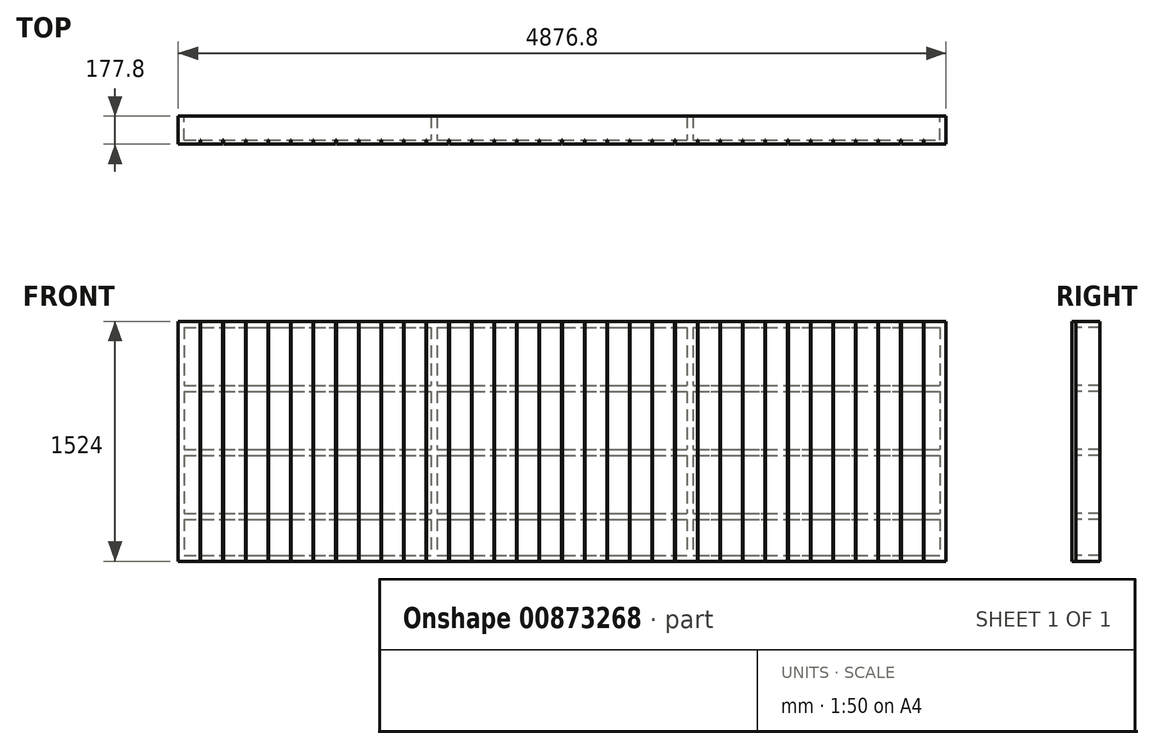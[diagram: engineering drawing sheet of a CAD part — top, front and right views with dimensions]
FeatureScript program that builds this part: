
annotation { "Feature Type Name" : "Feature", "Feature Type Description" : "" }
export const myFeature = defineFeature(function(context is Context, id is Id, definition is map)
    precondition{}
    {
        {
            var Q0;
            Q0=qCreatedBy(makeId("Front.planeOp"),FACE);
            var sketch = newSketch(context, id + "F0", { "sketchPlane" : qUnion([Q0])});
            skLineSegment(sketch, "E0.bottom", {"start": v(0, 0) * mm, "end": v(4876.8, 0) * mm});
            skLineSegment(sketch, "E0.top", {"start": v(0, -1524) * mm, "end": v(4876.8, -1524) * mm});
            skLineSegment(sketch, "E0.left", {"start": v(0, 0) * mm, "end": v(0, -1524) * mm});
            skLineSegment(sketch, "E0.right", {"start": v(4876.8, 0) * mm, "end": v(4876.8, -1524) * mm});
            skLineSegment(sketch, "E1.bottom", {"start": v(38.1, -38.1) * mm, "end": v(4838.7, -38.1) * mm});
            skLineSegment(sketch, "E1.top", {"start": v(38.1, -406.4) * mm, "end": v(4838.7, -406.4) * mm});
            skLineSegment(sketch, "E1.left", {"start": v(38.1, -38.1) * mm, "end": v(38.1, -406.4) * mm});
            skLineSegment(sketch, "E1.right", {"start": v(4838.7, -38.1) * mm, "end": v(4838.7, -406.4) * mm});
            skLineSegment(sketch, "E2", {"start": v(0, -425.45) * mm, "end": v(4876.8, -425.45) * mm, "construction": true});
            skLineSegment(sketch, "E3", {"start": v(4876.8, -19.05) * mm, "end": v(0, -19.05) * mm, "construction": true});
            skLineSegment(sketch, "E4.0.1.0", {"start": v(38.1, -812.8) * mm, "end": v(4838.7, -812.8) * mm});
            skLineSegment(sketch, "E4.0.1.1", {"start": v(38.1, -444.5) * mm, "end": v(38.1, -812.8) * mm});
            skLineSegment(sketch, "E4.0.1.2", {"start": v(38.1, -444.5) * mm, "end": v(4838.7, -444.5) * mm});
            skLineSegment(sketch, "E4.0.1.3", {"start": v(4838.7, -444.5) * mm, "end": v(4838.7, -812.8) * mm});
            skLineSegment(sketch, "E4.0.2.0", {"start": v(38.1, -1219.2) * mm, "end": v(4838.7, -1219.2) * mm});
            skLineSegment(sketch, "E4.0.2.1", {"start": v(38.1, -850.9) * mm, "end": v(38.1, -1219.2) * mm});
            skLineSegment(sketch, "E4.0.2.2", {"start": v(38.1, -850.9) * mm, "end": v(4838.7, -850.9) * mm});
            skLineSegment(sketch, "E4.0.2.3", {"start": v(4838.7, -850.9) * mm, "end": v(4838.7, -1219.2) * mm});
            skLineSegment(sketch, "E4.direction1", {"start": v(38.1, -406.4) * mm, "end": v(63.5, -406.4) * mm, "construction": true});
            skLineSegment(sketch, "E4.direction2", {"start": v(38.1, -406.4) * mm, "end": v(38.1, -812.8) * mm, "construction": true});
            skLineSegment(sketch, "E5.bottom", {"start": v(38.1, -1257.3) * mm, "end": v(4838.7, -1257.3) * mm});
            skLineSegment(sketch, "E5.top", {"start": v(38.1, -1485.9) * mm, "end": v(4838.7, -1485.9) * mm});
            skLineSegment(sketch, "E5.left", {"start": v(38.1, -1257.3) * mm, "end": v(38.1, -1485.9) * mm});
            skLineSegment(sketch, "E5.right", {"start": v(4838.7, -1257.3) * mm, "end": v(4838.7, -1485.9) * mm});
            skSolve(sketch);
        }
        {
            var Q0;
            Q0 = qSketchRegion(id + "F0", true);
            extrude(context, id + "F1", {"entities" : qUnion([Q0]), "depth" : 152.4 * mm, "offsetDistance" : 25.4 * mm});
        }
        {
            var Q0;
            Q0=makeQuery(id+"F1.opExtrude","CAP_FACE",FACE,{"disambiguationData":[OSD([sQuery(id+"F0.wireOp",EDGE,"E0.bottom"),sQuery(id+"F0.wireOp",EDGE,"E0.top"),sQuery(id+"F0.wireOp",EDGE,"E0.left"),sQuery(id+"F0.wireOp",EDGE,"E0.right"),sQuery(id+"F0.wireOp",EDGE,"E1.bottom"),sQuery(id+"F0.wireOp",EDGE,"E1.top"),sQuery(id+"F0.wireOp",EDGE,"E1.left"),sQuery(id+"F0.wireOp",EDGE,"E1.right"),sQuery(id+"F0.wireOp",EDGE,"E4.0.1.0"),sQuery(id+"F0.wireOp",EDGE,"E4.0.1.1"),sQuery(id+"F0.wireOp",EDGE,"E4.0.1.2"),sQuery(id+"F0.wireOp",EDGE,"E4.0.1.3"),sQuery(id+"F0.wireOp",EDGE,"E4.0.2.0"),sQuery(id+"F0.wireOp",EDGE,"E4.0.2.1"),sQuery(id+"F0.wireOp",EDGE,"E4.0.2.2"),sQuery(id+"F0.wireOp",EDGE,"E4.0.2.3"),sQuery(id+"F0.wireOp",EDGE,"E5.bottom"),sQuery(id+"F0.wireOp",EDGE,"E5.top"),sQuery(id+"F0.wireOp",EDGE,"E5.left"),sQuery(id+"F0.wireOp",EDGE,"E5.right")])],"isStart":false});
            var sketch = newSketch(context, id + "F2", { "sketchPlane" : qUnion([Q0])});
            skLineSegment(sketch, "E6", {"start": v(1625.6, 0) * mm, "end": v(1625.6, -1524) * mm, "construction": true});
            skLineSegment(sketch, "E7", {"start": v(3251.2, 0) * mm, "end": v(3251.2, -1524) * mm, "construction": true});
            skLineSegment(sketch, "E8.0", {"start": v(1606.55, 0) * mm, "end": v(1606.55, -1524) * mm});
            skLineSegment(sketch, "E9.0", {"start": v(1644.65, 0) * mm, "end": v(1644.65, -1524) * mm});
            skLineSegment(sketch, "E10.0", {"start": v(3232.15, 0) * mm, "end": v(3232.15, -1524) * mm});
            skLineSegment(sketch, "E11.0", {"start": v(3270.25, 0) * mm, "end": v(3270.25, -1524) * mm});
            skSolve(sketch);
        }
        {
            var Q0;
            Q0 = qSketchRegion(id + "F2", true);
            var Q1;
            {var subQ0=sQuery(id+"F2.wireOp",EDGE,"E8.0");var subQ1=makeQuery(id+"F1.opExtrude","CAP_EDGE",EDGE,{"disambiguationData":[OSD([sQuery(id+"F0.wireOp",EDGE,"E4.0.2.2")])],"isStart":false});var subQ2=makeQuery(id+"F2.imprint","INTERSECT",VERTEX,{"derivedFrom":[subQ1,subQ0]});Q1=makeQuery(id+"F2.imprint","IMPRINT",FACE,{"disambiguationData":[TD([[makeQuery(id+"F2.imprint","IMPRINT",EDGE,{"disambiguationData":[TD([[subQ2,-1.0]])],"derivedFrom":subQ0}),1.0]])]});}
            var Q2;
            {var subQ0=sQuery(id+"F2.wireOp",EDGE,"E8.0");var subQ1=makeQuery(id+"F1.opExtrude","CAP_EDGE",EDGE,{"disambiguationData":[OSD([sQuery(id+"F0.wireOp",EDGE,"E4.0.1.2")])],"isStart":false});var subQ2=makeQuery(id+"F2.imprint","INTERSECT",VERTEX,{"derivedFrom":[subQ1,subQ0]});Q2=makeQuery(id+"F2.imprint","IMPRINT",FACE,{"disambiguationData":[TD([[makeQuery(id+"F2.imprint","IMPRINT",EDGE,{"disambiguationData":[TD([[subQ2,-1.0]])],"derivedFrom":subQ0}),1.0]])]});}
            var Q3;
            {var subQ0=sQuery(id+"F2.wireOp",EDGE,"E8.0");var subQ1=makeQuery(id+"F1.opExtrude","CAP_EDGE",EDGE,{"disambiguationData":[OSD([sQuery(id+"F0.wireOp",EDGE,"E1.bottom")])],"isStart":false});var subQ2=makeQuery(id+"F2.imprint","INTERSECT",VERTEX,{"derivedFrom":[subQ1,subQ0]});Q3=makeQuery(id+"F2.imprint","IMPRINT",FACE,{"disambiguationData":[TD([[makeQuery(id+"F2.imprint","IMPRINT",EDGE,{"disambiguationData":[TD([[subQ2,-1.0]])],"derivedFrom":subQ0}),1.0]])]});}
            var Q4;
            {var subQ0=sQuery(id+"F2.wireOp",EDGE,"E8.0");var subQ1=makeQuery(id+"F1.opExtrude","CAP_EDGE",EDGE,{"disambiguationData":[OSD([sQuery(id+"F0.wireOp",EDGE,"E5.bottom")])],"isStart":false});var subQ2=makeQuery(id+"F2.imprint","INTERSECT",VERTEX,{"derivedFrom":[subQ1,subQ0]});Q4=makeQuery(id+"F2.imprint","IMPRINT",FACE,{"disambiguationData":[TD([[makeQuery(id+"F2.imprint","IMPRINT",EDGE,{"disambiguationData":[TD([[subQ2,-1.0]])],"derivedFrom":subQ0}),1.0]])]});}
            var Q5;
            {var subQ0=sQuery(id+"F2.wireOp",EDGE,"E10.0");var subQ1=makeQuery(id+"F1.opExtrude","CAP_EDGE",EDGE,{"disambiguationData":[OSD([sQuery(id+"F0.wireOp",EDGE,"E5.bottom")])],"isStart":false});var subQ2=makeQuery(id+"F2.imprint","INTERSECT",VERTEX,{"derivedFrom":[subQ1,subQ0]});Q5=makeQuery(id+"F2.imprint","IMPRINT",FACE,{"disambiguationData":[TD([[makeQuery(id+"F2.imprint","IMPRINT",EDGE,{"disambiguationData":[TD([[subQ2,-1.0]])],"derivedFrom":subQ0}),1.0]])]});}
            var Q6;
            {var subQ0=sQuery(id+"F2.wireOp",EDGE,"E10.0");var subQ1=makeQuery(id+"F1.opExtrude","CAP_EDGE",EDGE,{"disambiguationData":[OSD([sQuery(id+"F0.wireOp",EDGE,"E4.0.2.2")])],"isStart":false});var subQ2=makeQuery(id+"F2.imprint","INTERSECT",VERTEX,{"derivedFrom":[subQ1,subQ0]});Q6=makeQuery(id+"F2.imprint","IMPRINT",FACE,{"disambiguationData":[TD([[makeQuery(id+"F2.imprint","IMPRINT",EDGE,{"disambiguationData":[TD([[subQ2,-1.0]])],"derivedFrom":subQ0}),1.0]])]});}
            var Q7;
            {var subQ0=sQuery(id+"F2.wireOp",EDGE,"E10.0");var subQ1=makeQuery(id+"F1.opExtrude","CAP_EDGE",EDGE,{"disambiguationData":[OSD([sQuery(id+"F0.wireOp",EDGE,"E4.0.1.2")])],"isStart":false});var subQ2=makeQuery(id+"F2.imprint","INTERSECT",VERTEX,{"derivedFrom":[subQ1,subQ0]});Q7=makeQuery(id+"F2.imprint","IMPRINT",FACE,{"disambiguationData":[TD([[makeQuery(id+"F2.imprint","IMPRINT",EDGE,{"disambiguationData":[TD([[subQ2,-1.0]])],"derivedFrom":subQ0}),1.0]])]});}
            var Q8;
            {var subQ0=sQuery(id+"F2.wireOp",EDGE,"E10.0");var subQ1=makeQuery(id+"F1.opExtrude","CAP_EDGE",EDGE,{"disambiguationData":[OSD([sQuery(id+"F0.wireOp",EDGE,"E1.bottom")])],"isStart":false});var subQ2=makeQuery(id+"F2.imprint","INTERSECT",VERTEX,{"derivedFrom":[subQ1,subQ0]});Q8=makeQuery(id+"F2.imprint","IMPRINT",FACE,{"disambiguationData":[TD([[makeQuery(id+"F2.imprint","IMPRINT",EDGE,{"disambiguationData":[TD([[subQ2,-1.0]])],"derivedFrom":subQ0}),1.0]])]});}
            extrude(context, id + "F3", {"entities" : qUnion([Q0, Q1, Q2, Q3, Q4, Q5, Q6, Q7, Q8]), "operationType" : NewBodyOperationType.ADD, "oppositeDirection" : true, "depth" : 152.4 * mm, "offsetDistance" : 25.4 * mm});
        }
        {
            var Q0;
            {var subQ0=sQuery(id+"F2.wireOp",EDGE,"E11.0");var subQ1=sQuery(id+"F2.wireOp",EDGE,"E10.0");var subQ2=sQuery(id+"F0.wireOp",EDGE,"E5.top");var subQ3=sQuery(id+"F0.wireOp",EDGE,"E5.bottom");var subQ4=sQuery(id+"F0.wireOp",EDGE,"E4.0.2.2");var subQ5=sQuery(id+"F0.wireOp",EDGE,"E4.0.2.0");var subQ6=sQuery(id+"F0.wireOp",EDGE,"E4.0.1.2");var subQ7=sQuery(id+"F0.wireOp",EDGE,"E4.0.1.0");var subQ8=sQuery(id+"F0.wireOp",EDGE,"E1.top");var subQ9=sQuery(id+"F0.wireOp",EDGE,"E1.bottom");var subQ10=sQuery(id+"F2.wireOp",EDGE,"E9.0");var subQ11=sQuery(id+"F2.wireOp",EDGE,"E8.0");Q0=makeQuery(id+"F3.boolean.opBoolean","MERGE",FACE,{"derivedFrom":[makeQuery(id+"F1.opExtrude","CAP_FACE",FACE,{"disambiguationData":[OSD([sQuery(id+"F0.wireOp",EDGE,"E0.bottom"),sQuery(id+"F0.wireOp",EDGE,"E0.top"),sQuery(id+"F0.wireOp",EDGE,"E0.left"),sQuery(id+"F0.wireOp",EDGE,"E0.right"),subQ9,subQ8,sQuery(id+"F0.wireOp",EDGE,"E1.left"),sQuery(id+"F0.wireOp",EDGE,"E1.right"),subQ7,sQuery(id+"F0.wireOp",EDGE,"E4.0.1.1"),subQ6,sQuery(id+"F0.wireOp",EDGE,"E4.0.1.3"),subQ5,sQuery(id+"F0.wireOp",EDGE,"E4.0.2.1"),subQ4,sQuery(id+"F0.wireOp",EDGE,"E4.0.2.3"),subQ3,subQ2,sQuery(id+"F0.wireOp",EDGE,"E5.left"),sQuery(id+"F0.wireOp",EDGE,"E5.right")])],"isStart":false}),makeQuery(id+"F3.opExtrude","CAP_FACE",FACE,{"disambiguationData":[OSD([subQ9,subQ8,subQ11,subQ10])],"isStart":true}),makeQuery(id+"F3.opExtrude","CAP_FACE",FACE,{"disambiguationData":[OSD([subQ7,subQ6,subQ11,subQ10])],"isStart":true}),makeQuery(id+"F3.opExtrude","CAP_FACE",FACE,{"disambiguationData":[OSD([subQ5,subQ4,subQ11,subQ10])],"isStart":true}),makeQuery(id+"F3.opExtrude","CAP_FACE",FACE,{"disambiguationData":[OSD([subQ3,subQ2,subQ11,subQ10])],"isStart":true}),makeQuery(id+"F3.opExtrude","CAP_FACE",FACE,{"disambiguationData":[OSD([subQ9,subQ8,subQ1,subQ0])],"isStart":true}),makeQuery(id+"F3.opExtrude","CAP_FACE",FACE,{"disambiguationData":[OSD([subQ7,subQ6,subQ1,subQ0])],"isStart":true}),makeQuery(id+"F3.opExtrude","CAP_FACE",FACE,{"disambiguationData":[OSD([subQ5,subQ4,subQ1,subQ0])],"isStart":true}),makeQuery(id+"F3.opExtrude","CAP_FACE",FACE,{"disambiguationData":[OSD([subQ3,subQ2,subQ1,subQ0])],"isStart":true})]});}
            var sketch = newSketch(context, id + "F4", { "sketchPlane" : qUnion([Q0])});
            skLineSegment(sketch, "E12.bottom", {"start": v(0, 0) * mm, "end": v(139.7, 0) * mm});
            skLineSegment(sketch, "E12.top", {"start": v(0, -1524) * mm, "end": v(139.7, -1524) * mm});
            skLineSegment(sketch, "E12.left", {"start": v(0, 0) * mm, "end": v(0, -1524) * mm});
            skLineSegment(sketch, "E12.right", {"start": v(139.7, 0) * mm, "end": v(139.7, -1524) * mm});
            skLineSegment(sketch, "E13.1.0.0", {"start": v(143.5, 0) * mm, "end": v(283.21, 0) * mm});
            skLineSegment(sketch, "E13.1.0.1", {"start": v(283.21, 0) * mm, "end": v(283.21, -1524) * mm});
            skLineSegment(sketch, "E13.1.0.2", {"start": v(143.5, 0) * mm, "end": v(143.51, -1524) * mm});
            skLineSegment(sketch, "E13.1.0.3", {"start": v(143.51, -1524) * mm, "end": v(283.21, -1524) * mm});
            skLineSegment(sketch, "E13.2.0.0", {"start": v(287.02, 0) * mm, "end": v(426.72, 0) * mm});
            skLineSegment(sketch, "E13.2.0.1", {"start": v(426.72, 0) * mm, "end": v(426.72, -1524) * mm});
            skLineSegment(sketch, "E13.2.0.2", {"start": v(287.02, 0) * mm, "end": v(287.02, -1524) * mm});
            skLineSegment(sketch, "E13.2.0.3", {"start": v(287.02, -1524) * mm, "end": v(426.72, -1524) * mm});
            skLineSegment(sketch, "E13.3.0.0", {"start": v(430.53, 0) * mm, "end": v(570.23, 0) * mm});
            skLineSegment(sketch, "E13.3.0.1", {"start": v(570.23, 0) * mm, "end": v(570.23, -1524) * mm});
            skLineSegment(sketch, "E13.3.0.2", {"start": v(430.53, 0) * mm, "end": v(430.53, -1524) * mm});
            skLineSegment(sketch, "E13.3.0.3", {"start": v(430.53, -1524) * mm, "end": v(570.23, -1524) * mm});
            skLineSegment(sketch, "E13.4.0.0", {"start": v(574.04, 0) * mm, "end": v(713.74, 0) * mm});
            skLineSegment(sketch, "E13.4.0.1", {"start": v(713.74, 0) * mm, "end": v(713.74, -1524) * mm});
            skLineSegment(sketch, "E13.4.0.2", {"start": v(574.04, 0) * mm, "end": v(574.04, -1524) * mm});
            skLineSegment(sketch, "E13.4.0.3", {"start": v(574.04, -1524) * mm, "end": v(713.74, -1524) * mm});
            skLineSegment(sketch, "E13.5.0.0", {"start": v(717.55, 0) * mm, "end": v(857.25, 0) * mm});
            skLineSegment(sketch, "E13.5.0.1", {"start": v(857.25, 0) * mm, "end": v(857.25, -1524) * mm});
            skLineSegment(sketch, "E13.5.0.2", {"start": v(717.55, 0) * mm, "end": v(717.55, -1524) * mm});
            skLineSegment(sketch, "E13.5.0.3", {"start": v(717.55, -1524) * mm, "end": v(857.25, -1524) * mm});
            skLineSegment(sketch, "E13.6.0.0", {"start": v(861.06, 0) * mm, "end": v(1000.76, 0) * mm});
            skLineSegment(sketch, "E13.6.0.1", {"start": v(1000.76, 0) * mm, "end": v(1000.76, -1524) * mm});
            skLineSegment(sketch, "E13.6.0.2", {"start": v(861.06, 0) * mm, "end": v(861.06, -1524) * mm});
            skLineSegment(sketch, "E13.6.0.3", {"start": v(861.06, -1524) * mm, "end": v(1000.76, -1524) * mm});
            skLineSegment(sketch, "E13.7.0.0", {"start": v(1004.57, 0) * mm, "end": v(1144.27, 0) * mm});
            skLineSegment(sketch, "E13.7.0.1", {"start": v(1144.27, 0) * mm, "end": v(1144.27, -1524) * mm});
            skLineSegment(sketch, "E13.7.0.2", {"start": v(1004.57, 0) * mm, "end": v(1004.57, -1524) * mm});
            skLineSegment(sketch, "E13.7.0.3", {"start": v(1004.57, -1524) * mm, "end": v(1144.27, -1524) * mm});
            skLineSegment(sketch, "E13.8.0.0", {"start": v(1148.08, 0) * mm, "end": v(1287.78, 0) * mm});
            skLineSegment(sketch, "E13.8.0.1", {"start": v(1287.78, 0) * mm, "end": v(1287.78, -1524) * mm});
            skLineSegment(sketch, "E13.8.0.2", {"start": v(1148.08, 0) * mm, "end": v(1148.08, -1524) * mm});
            skLineSegment(sketch, "E13.8.0.3", {"start": v(1148.08, -1524) * mm, "end": v(1287.78, -1524) * mm});
            skLineSegment(sketch, "E13.9.0.0", {"start": v(1291.6, 0) * mm, "end": v(1431.3, 0) * mm});
            skLineSegment(sketch, "E13.9.0.1", {"start": v(1431.3, 0) * mm, "end": v(1431.3, -1524) * mm});
            skLineSegment(sketch, "E13.9.0.2", {"start": v(1291.6, 0) * mm, "end": v(1291.6, -1524) * mm});
            skLineSegment(sketch, "E13.9.0.3", {"start": v(1291.6, -1524) * mm, "end": v(1431.3, -1524) * mm});
            skLineSegment(sketch, "E13.10.0.0", {"start": v(1435.1, 0) * mm, "end": v(1574.8, 0) * mm});
            skLineSegment(sketch, "E13.10.0.1", {"start": v(1574.8, 0) * mm, "end": v(1574.8, -1524) * mm});
            skLineSegment(sketch, "E13.10.0.2", {"start": v(1435.1, 0) * mm, "end": v(1435.1, -1524) * mm});
            skLineSegment(sketch, "E13.10.0.3", {"start": v(1435.1, -1524) * mm, "end": v(1574.8, -1524) * mm});
            skLineSegment(sketch, "E13.11.0.0", {"start": v(1578.61, 0) * mm, "end": v(1718.3, 0) * mm});
            skLineSegment(sketch, "E13.11.0.1", {"start": v(1718.31, 0) * mm, "end": v(1718.31, -1524) * mm});
            skLineSegment(sketch, "E13.11.0.2", {"start": v(1578.61, 0) * mm, "end": v(1578.61, -1524) * mm});
            skLineSegment(sketch, "E13.11.0.3", {"start": v(1578.61, -1524) * mm, "end": v(1718.31, -1524) * mm});
            skLineSegment(sketch, "E13.12.0.0", {"start": v(1722.12, 0) * mm, "end": v(1861.82, 0) * mm});
            skLineSegment(sketch, "E13.12.0.1", {"start": v(1861.82, 0) * mm, "end": v(1861.82, -1524) * mm});
            skLineSegment(sketch, "E13.12.0.2", {"start": v(1722.12, 0) * mm, "end": v(1722.12, -1524) * mm});
            skLineSegment(sketch, "E13.12.0.3", {"start": v(1722.12, -1524) * mm, "end": v(1861.82, -1524) * mm});
            skLineSegment(sketch, "E13.13.0.0", {"start": v(1865.63, 0) * mm, "end": v(2005.33, 0) * mm});
            skLineSegment(sketch, "E13.13.0.1", {"start": v(2005.33, 0) * mm, "end": v(2005.33, -1524) * mm});
            skLineSegment(sketch, "E13.13.0.2", {"start": v(1865.63, 0) * mm, "end": v(1865.63, -1524) * mm});
            skLineSegment(sketch, "E13.13.0.3", {"start": v(1865.63, -1524) * mm, "end": v(2005.33, -1524) * mm});
            skLineSegment(sketch, "E13.14.0.0", {"start": v(2009.14, 0) * mm, "end": v(2148.84, 0) * mm});
            skLineSegment(sketch, "E13.14.0.1", {"start": v(2148.84, 0) * mm, "end": v(2148.84, -1524) * mm});
            skLineSegment(sketch, "E13.14.0.2", {"start": v(2009.14, 0) * mm, "end": v(2009.14, -1524) * mm});
            skLineSegment(sketch, "E13.14.0.3", {"start": v(2009.14, -1524) * mm, "end": v(2148.84, -1524) * mm});
            skLineSegment(sketch, "E13.15.0.0", {"start": v(2152.65, 0) * mm, "end": v(2292.35, 0) * mm});
            skLineSegment(sketch, "E13.15.0.1", {"start": v(2292.35, 0) * mm, "end": v(2292.35, -1524) * mm});
            skLineSegment(sketch, "E13.15.0.2", {"start": v(2152.65, 0) * mm, "end": v(2152.65, -1524) * mm});
            skLineSegment(sketch, "E13.15.0.3", {"start": v(2152.65, -1524) * mm, "end": v(2292.35, -1524) * mm});
            skLineSegment(sketch, "E13.16.0.0", {"start": v(2296.16, 0) * mm, "end": v(2435.86, 0) * mm});
            skLineSegment(sketch, "E13.16.0.1", {"start": v(2435.86, 0) * mm, "end": v(2435.86, -1524) * mm});
            skLineSegment(sketch, "E13.16.0.2", {"start": v(2296.16, 0) * mm, "end": v(2296.16, -1524) * mm});
            skLineSegment(sketch, "E13.16.0.3", {"start": v(2296.16, -1524) * mm, "end": v(2435.86, -1524) * mm});
            skLineSegment(sketch, "E13.17.0.0", {"start": v(2439.67, 0) * mm, "end": v(2579.37, 0) * mm});
            skLineSegment(sketch, "E13.17.0.1", {"start": v(2579.37, 0) * mm, "end": v(2579.37, -1524) * mm});
            skLineSegment(sketch, "E13.17.0.2", {"start": v(2439.67, 0) * mm, "end": v(2439.67, -1524) * mm});
            skLineSegment(sketch, "E13.17.0.3", {"start": v(2439.67, -1524) * mm, "end": v(2579.37, -1524) * mm});
            skLineSegment(sketch, "E13.18.0.0", {"start": v(2583.18, 0) * mm, "end": v(2722.88, 0) * mm});
            skLineSegment(sketch, "E13.18.0.1", {"start": v(2722.88, 0) * mm, "end": v(2722.88, -1524) * mm});
            skLineSegment(sketch, "E13.18.0.2", {"start": v(2583.18, 0) * mm, "end": v(2583.18, -1524) * mm});
            skLineSegment(sketch, "E13.18.0.3", {"start": v(2583.18, -1524) * mm, "end": v(2722.88, -1524) * mm});
            skLineSegment(sketch, "E13.19.0.0", {"start": v(2726.7, 0) * mm, "end": v(2866.39, 0) * mm});
            skLineSegment(sketch, "E13.19.0.1", {"start": v(2866.39, 0) * mm, "end": v(2866.39, -1524) * mm});
            skLineSegment(sketch, "E13.19.0.2", {"start": v(2726.7, 0) * mm, "end": v(2726.7, -1524) * mm});
            skLineSegment(sketch, "E13.19.0.3", {"start": v(2726.7, -1524) * mm, "end": v(2866.39, -1524) * mm});
            skLineSegment(sketch, "E13.20.0.0", {"start": v(2870.2, 0) * mm, "end": v(3009.9, 0) * mm});
            skLineSegment(sketch, "E13.20.0.1", {"start": v(3009.9, 0) * mm, "end": v(3009.9, -1524) * mm});
            skLineSegment(sketch, "E13.20.0.2", {"start": v(2870.2, 0) * mm, "end": v(2870.2, -1524) * mm});
            skLineSegment(sketch, "E13.20.0.3", {"start": v(2870.2, -1524) * mm, "end": v(3009.9, -1524) * mm});
            skLineSegment(sketch, "E13.21.0.0", {"start": v(3013.71, 0) * mm, "end": v(3153.4, 0) * mm});
            skLineSegment(sketch, "E13.21.0.1", {"start": v(3153.4, 0) * mm, "end": v(3153.4, -1524) * mm});
            skLineSegment(sketch, "E13.21.0.2", {"start": v(3013.71, 0) * mm, "end": v(3013.71, -1524) * mm});
            skLineSegment(sketch, "E13.21.0.3", {"start": v(3013.71, -1524) * mm, "end": v(3153.4, -1524) * mm});
            skLineSegment(sketch, "E13.22.0.0", {"start": v(3157.22, 0) * mm, "end": v(3296.92, 0) * mm});
            skLineSegment(sketch, "E13.22.0.1", {"start": v(3296.92, 0) * mm, "end": v(3296.92, -1524) * mm});
            skLineSegment(sketch, "E13.22.0.2", {"start": v(3157.22, 0) * mm, "end": v(3157.22, -1524) * mm});
            skLineSegment(sketch, "E13.22.0.3", {"start": v(3157.22, -1524) * mm, "end": v(3296.92, -1524) * mm});
            skLineSegment(sketch, "E13.23.0.0", {"start": v(3300.73, 0) * mm, "end": v(3440.43, 0) * mm});
            skLineSegment(sketch, "E13.23.0.1", {"start": v(3440.43, 0) * mm, "end": v(3440.43, -1524) * mm});
            skLineSegment(sketch, "E13.23.0.2", {"start": v(3300.73, 0) * mm, "end": v(3300.73, -1524) * mm});
            skLineSegment(sketch, "E13.23.0.3", {"start": v(3300.73, -1524) * mm, "end": v(3440.43, -1524) * mm});
            skLineSegment(sketch, "E13.24.0.0", {"start": v(3444.24, 0) * mm, "end": v(3583.94, 0) * mm});
            skLineSegment(sketch, "E13.24.0.1", {"start": v(3583.94, 0) * mm, "end": v(3583.94, -1524) * mm});
            skLineSegment(sketch, "E13.24.0.2", {"start": v(3444.24, 0) * mm, "end": v(3444.24, -1524) * mm});
            skLineSegment(sketch, "E13.24.0.3", {"start": v(3444.24, -1524) * mm, "end": v(3583.94, -1524) * mm});
            skLineSegment(sketch, "E13.25.0.0", {"start": v(3587.75, 0) * mm, "end": v(3727.45, 0) * mm});
            skLineSegment(sketch, "E13.25.0.1", {"start": v(3727.45, 0) * mm, "end": v(3727.45, -1524) * mm});
            skLineSegment(sketch, "E13.25.0.2", {"start": v(3587.75, 0) * mm, "end": v(3587.75, -1524) * mm});
            skLineSegment(sketch, "E13.25.0.3", {"start": v(3587.75, -1524) * mm, "end": v(3727.45, -1524) * mm});
            skLineSegment(sketch, "E13.26.0.0", {"start": v(3731.26, 0) * mm, "end": v(3870.96, 0) * mm});
            skLineSegment(sketch, "E13.26.0.1", {"start": v(3870.96, 0) * mm, "end": v(3870.96, -1524) * mm});
            skLineSegment(sketch, "E13.26.0.2", {"start": v(3731.26, 0) * mm, "end": v(3731.26, -1524) * mm});
            skLineSegment(sketch, "E13.26.0.3", {"start": v(3731.26, -1524) * mm, "end": v(3870.96, -1524) * mm});
            skLineSegment(sketch, "E13.27.0.0", {"start": v(3874.77, 0) * mm, "end": v(4014.47, 0) * mm});
            skLineSegment(sketch, "E13.27.0.1", {"start": v(4014.47, 0) * mm, "end": v(4014.47, -1524) * mm});
            skLineSegment(sketch, "E13.27.0.2", {"start": v(3874.77, 0) * mm, "end": v(3874.77, -1524) * mm});
            skLineSegment(sketch, "E13.27.0.3", {"start": v(3874.77, -1524) * mm, "end": v(4014.47, -1524) * mm});
            skLineSegment(sketch, "E13.28.0.0", {"start": v(4018.28, 0) * mm, "end": v(4157.98, 0) * mm});
            skLineSegment(sketch, "E13.28.0.1", {"start": v(4157.98, 0) * mm, "end": v(4157.98, -1524) * mm});
            skLineSegment(sketch, "E13.28.0.2", {"start": v(4018.28, 0) * mm, "end": v(4018.28, -1524) * mm});
            skLineSegment(sketch, "E13.28.0.3", {"start": v(4018.28, -1524) * mm, "end": v(4157.98, -1524) * mm});
            skLineSegment(sketch, "E13.29.0.0", {"start": v(4161.79, 0) * mm, "end": v(4301.5, 0) * mm});
            skLineSegment(sketch, "E13.29.0.1", {"start": v(4301.5, 0) * mm, "end": v(4301.5, -1524) * mm});
            skLineSegment(sketch, "E13.29.0.2", {"start": v(4161.79, 0) * mm, "end": v(4161.79, -1524) * mm});
            skLineSegment(sketch, "E13.29.0.3", {"start": v(4161.79, -1524) * mm, "end": v(4301.5, -1524) * mm});
            skLineSegment(sketch, "E13.30.0.0", {"start": v(4305.3, 0) * mm, "end": v(4445, 0) * mm});
            skLineSegment(sketch, "E13.30.0.1", {"start": v(4445, 0) * mm, "end": v(4445, -1524) * mm});
            skLineSegment(sketch, "E13.30.0.2", {"start": v(4305.3, 0) * mm, "end": v(4305.3, -1524) * mm});
            skLineSegment(sketch, "E13.30.0.3", {"start": v(4305.3, -1524) * mm, "end": v(4445, -1524) * mm});
            skLineSegment(sketch, "E13.31.0.0", {"start": v(4448.8, 0) * mm, "end": v(4588.51, 0) * mm});
            skLineSegment(sketch, "E13.31.0.1", {"start": v(4588.51, 0) * mm, "end": v(4588.51, -1524) * mm});
            skLineSegment(sketch, "E13.31.0.2", {"start": v(4448.8, 0) * mm, "end": v(4448.8, -1524) * mm});
            skLineSegment(sketch, "E13.31.0.3", {"start": v(4448.8, -1524) * mm, "end": v(4588.51, -1524) * mm});
            skLineSegment(sketch, "E13.32.0.0", {"start": v(4592.32, 0) * mm, "end": v(4732.02, 0) * mm});
            skLineSegment(sketch, "E13.32.0.1", {"start": v(4732.02, 0) * mm, "end": v(4732.02, -1524) * mm});
            skLineSegment(sketch, "E13.32.0.2", {"start": v(4592.32, 0) * mm, "end": v(4592.32, -1524) * mm});
            skLineSegment(sketch, "E13.32.0.3", {"start": v(4592.32, -1524) * mm, "end": v(4732.02, -1524) * mm});
            skLineSegment(sketch, "E13.33.0.0", {"start": v(4735.83, 0) * mm, "end": v(4875.53, 0) * mm});
            skLineSegment(sketch, "E13.33.0.1", {"start": v(4875.53, 0) * mm, "end": v(4875.53, -1524) * mm});
            skLineSegment(sketch, "E13.33.0.2", {"start": v(4735.83, 0) * mm, "end": v(4735.83, -1524) * mm});
            skLineSegment(sketch, "E13.33.0.3", {"start": v(4735.83, -1524) * mm, "end": v(4875.53, -1524) * mm});
            skLineSegment(sketch, "E13.direction1", {"start": v(0, 0) * mm, "end": v(143.5, 0) * mm, "construction": true});
            skSolve(sketch);
        }
        {
            var Q0;
            Q0 = qSketchRegion(id + "F4", true);
            extrude(context, id + "F5", {"entities" : qUnion([Q0]), "operationType" : NewBodyOperationType.ADD, "depth" : 25.4 * mm, "offsetDistance" : 25.4 * mm});
        }
    });
